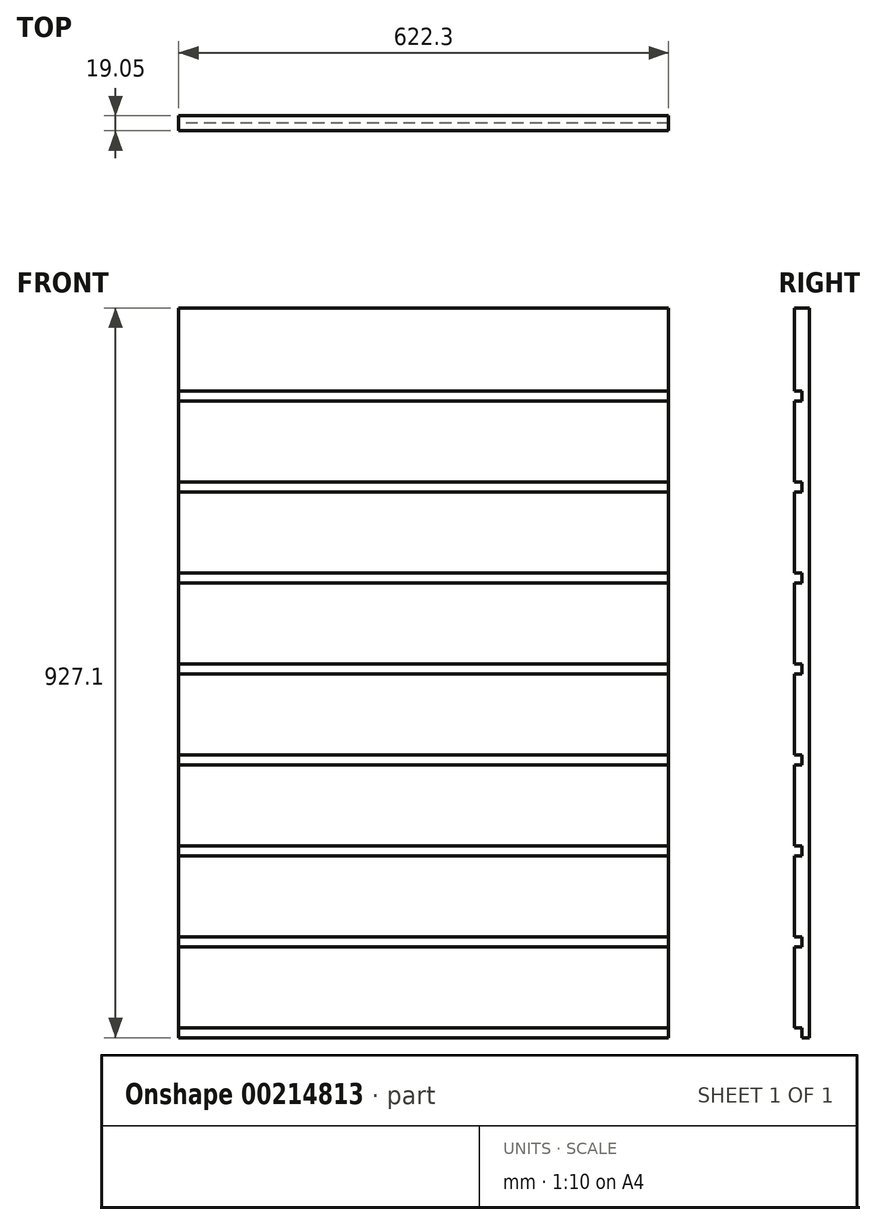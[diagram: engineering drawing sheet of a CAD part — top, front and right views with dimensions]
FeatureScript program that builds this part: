
annotation { "Feature Type Name" : "Feature", "Feature Type Description" : "" }
export const myFeature = defineFeature(function(context is Context, id is Id, definition is map)
    precondition{}
    {
        {
            var Q0;
            Q0=qCreatedBy(makeId("Front.planeOp"),FACE);
            var sketch = newSketch(context, id + "F0", { "sketchPlane" : qUnion([Q0])});
            skLineSegment(sketch, "E0.bottom", {"start": v(0, 0) * mm, "end": v(622.3, 0) * mm});
            skLineSegment(sketch, "E0.top", {"start": v(0, -927.1) * mm, "end": v(622.3, -927.1) * mm});
            skLineSegment(sketch, "E0.left", {"start": v(0, 0) * mm, "end": v(0, -927.1) * mm});
            skLineSegment(sketch, "E0.right", {"start": v(622.3, 0) * mm, "end": v(622.3, -927.1) * mm});
            skSolve(sketch);
        }
        {
            var Q0;
            Q0=makeQuery(id+"F0.imprint","IMPRINT",FACE,{"disambiguationData":[TD([[makeQuery(id+"F0.imprint","IMPRINT",EDGE,{"derivedFrom":sQuery(id+"F0.wireOp",EDGE,"E0.bottom")}),-1.0]])]});
            extrude(context, id + "F1", {"entities" : qUnion([Q0]), "depth" : 19.05 * mm});
        }
        {
            var Q0;
            Q0=makeQuery(id+"F1.opExtrude","SWEPT_FACE",FACE,{"disambiguationData":[OSD([sQuery(id+"F0.wireOp",EDGE,"E0.left")])]});
            var sketch = newSketch(context, id + "F2", { "sketchPlane" : qUnion([Q0])});
            skLineSegment(sketch, "E1.bottom", {"start": v(19.05, -105.4) * mm, "end": v(9.53, -105.4) * mm});
            skLineSegment(sketch, "E1.top", {"start": v(19.05, -118.1) * mm, "end": v(9.53, -118.1) * mm});
            skLineSegment(sketch, "E1.left", {"start": v(19.05, -105.4) * mm, "end": v(19.05, -118.1) * mm});
            skLineSegment(sketch, "E1.right", {"start": v(9.53, -105.4) * mm, "end": v(9.53, -118.1) * mm});
            skLineSegment(sketch, "E2.bottom", {"start": v(19.05, -220.98) * mm, "end": v(9.53, -220.98) * mm});
            skLineSegment(sketch, "E2.top", {"start": v(19.05, -233.68) * mm, "end": v(9.53, -233.68) * mm});
            skLineSegment(sketch, "E2.left", {"start": v(19.05, -220.98) * mm, "end": v(19.05, -233.68) * mm});
            skLineSegment(sketch, "E2.right", {"start": v(9.53, -220.98) * mm, "end": v(9.53, -233.68) * mm});
            skLineSegment(sketch, "E3.bottom", {"start": v(19.05, -336.55) * mm, "end": v(9.53, -336.55) * mm});
            skLineSegment(sketch, "E3.top", {"start": v(19.05, -349.25) * mm, "end": v(9.53, -349.25) * mm});
            skLineSegment(sketch, "E3.left", {"start": v(19.05, -336.55) * mm, "end": v(19.05, -349.25) * mm});
            skLineSegment(sketch, "E3.right", {"start": v(9.53, -336.55) * mm, "end": v(9.53, -349.25) * mm});
            skLineSegment(sketch, "E4.bottom", {"start": v(19.05, -452.12) * mm, "end": v(9.52, -452.12) * mm});
            skLineSegment(sketch, "E4.top", {"start": v(19.05, -464.82) * mm, "end": v(9.53, -464.82) * mm});
            skLineSegment(sketch, "E4.left", {"start": v(19.05, -452.12) * mm, "end": v(19.05, -464.82) * mm});
            skLineSegment(sketch, "E4.right", {"start": v(9.52, -452.12) * mm, "end": v(9.52, -464.82) * mm});
            skLineSegment(sketch, "E5.bottom", {"start": v(19.05, -567.69) * mm, "end": v(9.53, -567.69) * mm});
            skLineSegment(sketch, "E5.top", {"start": v(19.05, -580.39) * mm, "end": v(9.53, -580.39) * mm});
            skLineSegment(sketch, "E5.left", {"start": v(19.05, -567.69) * mm, "end": v(19.05, -580.39) * mm});
            skLineSegment(sketch, "E5.right", {"start": v(9.53, -567.69) * mm, "end": v(9.53, -580.39) * mm});
            skLineSegment(sketch, "E6.bottom", {"start": v(19.05, -683.26) * mm, "end": v(9.53, -683.26) * mm});
            skLineSegment(sketch, "E6.top", {"start": v(19.05, -695.96) * mm, "end": v(9.53, -695.96) * mm});
            skLineSegment(sketch, "E6.left", {"start": v(19.05, -683.26) * mm, "end": v(19.05, -695.96) * mm});
            skLineSegment(sketch, "E6.right", {"start": v(9.53, -683.26) * mm, "end": v(9.53, -695.96) * mm});
            skLineSegment(sketch, "E7.bottom", {"start": v(19.05, -798.83) * mm, "end": v(9.53, -798.83) * mm});
            skLineSegment(sketch, "E7.top", {"start": v(19.05, -811.53) * mm, "end": v(9.53, -811.53) * mm});
            skLineSegment(sketch, "E7.left", {"start": v(19.05, -798.83) * mm, "end": v(19.05, -811.53) * mm});
            skLineSegment(sketch, "E7.right", {"start": v(9.53, -798.83) * mm, "end": v(9.53, -811.53) * mm});
            skLineSegment(sketch, "E8.bottom", {"start": v(19.05, -914.4) * mm, "end": v(9.53, -914.4) * mm});
            skLineSegment(sketch, "E8.top", {"start": v(19.05, -927.1) * mm, "end": v(9.53, -927.1) * mm});
            skLineSegment(sketch, "E8.left", {"start": v(19.05, -914.4) * mm, "end": v(19.05, -927.1) * mm});
            skLineSegment(sketch, "E8.right", {"start": v(9.52, -914.4) * mm, "end": v(9.53, -927.1) * mm});
            skSolve(sketch);
        }
        {
            var Q0;
            Q0=makeQuery(id+"F2.imprint","IMPRINT",FACE,{"disambiguationData":[TD([[makeQuery(id+"F2.imprint","IMPRINT",EDGE,{"derivedFrom":sQuery(id+"F2.wireOp",EDGE,"E1.bottom")}),1.0]])]});
            var Q1;
            Q1=makeQuery(id+"F2.imprint","IMPRINT",FACE,{"disambiguationData":[TD([[makeQuery(id+"F2.imprint","IMPRINT",EDGE,{"derivedFrom":sQuery(id+"F2.wireOp",EDGE,"E2.bottom")}),1.0]])]});
            var Q2;
            Q2=makeQuery(id+"F2.imprint","IMPRINT",FACE,{"disambiguationData":[TD([[makeQuery(id+"F2.imprint","IMPRINT",EDGE,{"derivedFrom":sQuery(id+"F2.wireOp",EDGE,"E3.bottom")}),1.0]])]});
            var Q3;
            Q3=makeQuery(id+"F2.imprint","IMPRINT",FACE,{"disambiguationData":[TD([[makeQuery(id+"F2.imprint","IMPRINT",EDGE,{"derivedFrom":sQuery(id+"F2.wireOp",EDGE,"E4.bottom")}),1.0]])]});
            var Q4;
            Q4=makeQuery(id+"F2.imprint","IMPRINT",FACE,{"disambiguationData":[TD([[makeQuery(id+"F2.imprint","IMPRINT",EDGE,{"derivedFrom":sQuery(id+"F2.wireOp",EDGE,"E5.bottom")}),1.0]])]});
            var Q5;
            Q5=makeQuery(id+"F2.imprint","IMPRINT",FACE,{"disambiguationData":[TD([[makeQuery(id+"F2.imprint","IMPRINT",EDGE,{"derivedFrom":sQuery(id+"F2.wireOp",EDGE,"E6.bottom")}),1.0]])]});
            var Q6;
            Q6=makeQuery(id+"F2.imprint","IMPRINT",FACE,{"disambiguationData":[TD([[makeQuery(id+"F2.imprint","IMPRINT",EDGE,{"derivedFrom":sQuery(id+"F2.wireOp",EDGE,"E7.bottom")}),1.0]])]});
            var Q7;
            Q7=makeQuery(id+"F2.imprint","IMPRINT",FACE,{"disambiguationData":[TD([[makeQuery(id+"F2.imprint","IMPRINT",EDGE,{"derivedFrom":sQuery(id+"F2.wireOp",EDGE,"E8.bottom")}),1.0]])]});
            extrude(context, id + "F3", {"entities" : qUnion([Q0, Q1, Q2, Q3, Q4, Q5, Q6, Q7]), "operationType" : NewBodyOperationType.REMOVE, "oppositeDirection" : true, "depth" : 622.3 * mm});
        }
    });
